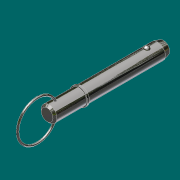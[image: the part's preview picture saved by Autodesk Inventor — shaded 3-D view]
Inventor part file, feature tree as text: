
AUTODESK INVENTOR PART (.ipt)
format: ipt  version: 2017 (Build 210142000, 142)  size: 156,160 bytes
history: native  units: in
note: dims shown in document units (in); Inventor stores cm internally (conversion verified against a paired STEP export)
features: sketch x5, extrude x2, chamfer x2, revolve x1, sweep x1
ambient origin geometry x8: Origin, YZ Plane, XZ Plane, XY Plane, X Axis, Y Axis, Z Axis, Center Point
bodies: Solid1 (feature_tree)
feature tree (11):
  extrude  "Extrusion1"  Depth=1.0625in TaperAngle=0.0deg
  extrude  "Extrusion2"  Depth=0.0625in TaperAngle=0.0deg
  chamfer  "Chamfer1"  Distance=0.1875in Angle=15.0deg
  chamfer  "Chamfer2"  Distance=0.0625in Angle=15.0deg
  revolve  "Revolution1"  [1 undecoded]
  sweep  "Sweep1"
  sketch  "Sketch1"  dims[d0=0.5in d1=1.0625in d2=2.625in d3=0.0in d4=0.0in]
  sketch  "Sketch2"  dims[d5=0.5625in d6=0.0625in d7=0.0in d8=0.1875in d9=0.125in d10=15.0deg d11=0.0625in d12=0.125in d13=15.0deg]
  sketch  "Sketch3"  dims[d14=0.1875in d15=2.0in]
  sketch  "Sketch4"  dims[d16=0.32in d17=90.0deg]
  sketch  "Sketch5"  dims[d18=1.25in d19=1.375in d20=0.0625in d21=0.0in d22=0.0in]
note: 1 required parameter value undecoded (feature->parameter linkage not recoverable at this tier; creation-order binding heuristic only, values carry confidence <= 0.55)
